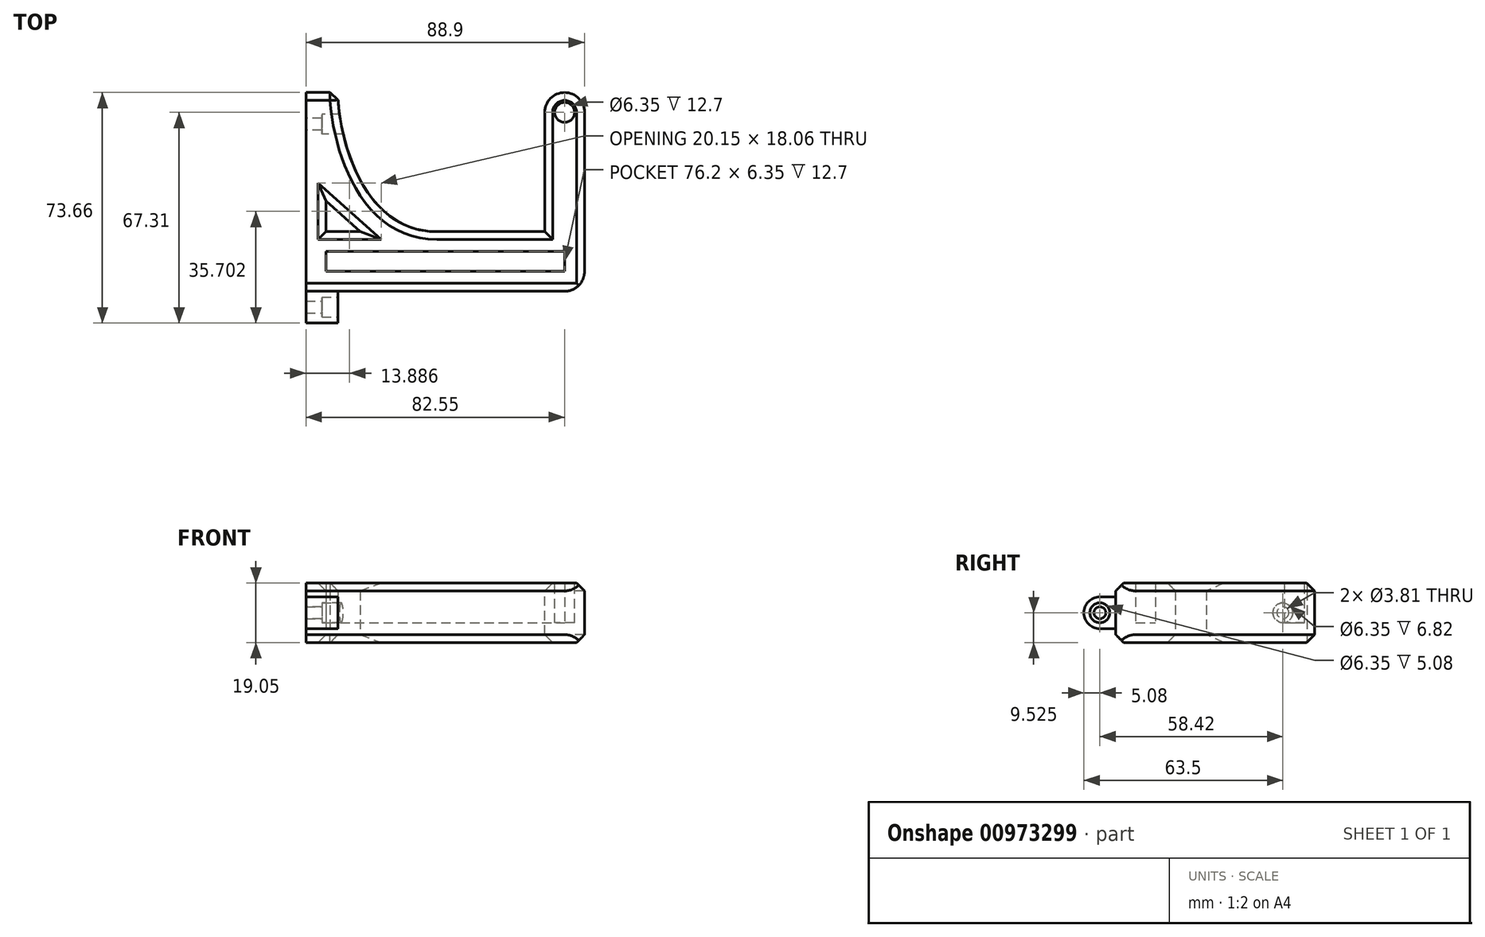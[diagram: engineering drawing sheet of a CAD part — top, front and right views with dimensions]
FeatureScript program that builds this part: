
annotation { "Feature Type Name" : "Feature", "Feature Type Description" : "" }
export const myFeature = defineFeature(function(context is Context, id is Id, definition is map)
    precondition{}
    {
        {
            var Q0;
            Q0=qCreatedBy(makeId("Top.planeOp"),FACE);
            var sketch = newSketch(context, id + "F0", { "sketchPlane" : qUnion([Q0])});
            skLineSegment(sketch, "E0.bottom", {"start": v(0, 0) * mm, "end": v(76.2, 0) * mm});
            skLineSegment(sketch, "E0.top", {"start": v(0, 6.35) * mm, "end": v(76.2, 6.35) * mm});
            skLineSegment(sketch, "E0.left", {"start": v(0, 0) * mm, "end": v(0, 6.35) * mm});
            skLineSegment(sketch, "E0.right", {"start": v(76.2, 0) * mm, "end": v(76.2, 6.35) * mm});
            skLineSegment(sketch, "E1.0", {"start": v(82.55, -6.35) * mm, "end": v(82.55, 12.7) * mm});
            skLineSegment(sketch, "E1.1", {"start": v(-6.35, -6.35) * mm, "end": v(82.55, -6.35) * mm});
            skLineSegment(sketch, "E1.2", {"start": v(-6.35, -6.35) * mm, "end": v(-6.35, 12.7) * mm});
            skLineSegment(sketch, "E1.3", {"start": v(31.6, 12.7) * mm, "end": v(82.55, 12.7) * mm});
            skLineSegment(sketch, "E2", {"start": v(-6.35, 12.7) * mm, "end": v(-6.35, 57.15) * mm});
            skLineSegment(sketch, "E3", {"start": v(-6.35, 57.15) * mm, "end": v(3.8, 57.15) * mm});
            skFitSpline(sketch, "E4", {"points": [v(3.8, 57.15) * mm, v(35.41, 12.7) * mm], "startDerivative": vector(0, -38.1) * mm, "endDerivative": vector(73.32, 0) * mm});
            skPoint(sketch, "E5.orphan", {"position": v(0, 12.7) * mm});
            skLineSegment(sketch, "E6", {"start": v(0, 22.54) * mm, "end": v(10.97, 12.7) * mm});
            skLineSegment(sketch, "E7", {"start": v(0, 22.54) * mm, "end": v(0, 12.7) * mm});
            skLineSegment(sketch, "E8", {"start": v(0, 12.7) * mm, "end": v(10.97, 12.7) * mm});
            skSolve(sketch);
        }
        {
            var Q0;
            Q0 = qSketchRegion(id + "F0", true);
            extrude(context, id + "F1", {"entities" : qUnion([Q0]), "depth" : 19.05 * mm, "offsetDistance" : 25.4 * mm});
        }
        {
            var Q0;
            Q0=makeQuery(id+"F0.imprint","IMPRINT",FACE,{"disambiguationData":[TD([[makeQuery(id+"F0.imprint","IMPRINT",EDGE,{"derivedFrom":sQuery(id+"F0.wireOp",EDGE,"E0.bottom")}),1.0]])]});
            extrude(context, id + "F2", {"entities" : qUnion([Q0]), "operationType" : NewBodyOperationType.ADD, "depth" : 6.35 * mm, "offsetDistance" : 25.4 * mm});
        }
        {
            var Q0;
            Q0=makeQuery(id+"F1.opExtrude","SWEPT_FACE",FACE,{"disambiguationData":[OSD([sQuery(id+"F0.wireOp",EDGE,"E1.2"),sQuery(id+"F0.wireOp",EDGE,"E2")])]});
            var sketch = newSketch(context, id + "F3", { "sketchPlane" : qUnion([Q0])});
            skCircle(sketch, "E9", {"center": v(-46.99, 9.53) * mm, "radius": 3.18 * mm});
            skPoint(sketch, "E9.centerSnap0", {"position": v(-57.15, 9.53) * mm});
            skCircle(sketch, "E10", {"center": v(-46.99, 9.53) * mm, "radius": 1.9 * mm});
            skSolve(sketch);
        }
        {
            var Q0;
            Q0=makeQuery(id+"F3.imprint","IMPRINT",FACE,{"disambiguationData":[TD([[makeQuery(id+"F3.imprint","IMPRINT",EDGE,{"derivedFrom":sQuery(id+"F3.wireOp",EDGE,"E9")}),1.0]])]});
            extrude(context, id + "F4", {"entities" : qUnion([Q0]), "operationType" : NewBodyOperationType.REMOVE, "endBound" : BoundingType.UP_TO_NEXT, "oppositeDirection" : true, "depth" : 25.4 * mm, "offsetDistance" : 25.4 * mm, "hasSecondDirection" : true, "secondDirectionOppositeDirection" : true, "secondDirectionDepth" : 5.08 * mm});
        }
        {
            var Q0;
            Q0=makeQuery(id+"F1.opExtrude","SWEPT_FACE",FACE,{"disambiguationData":[OSD([sQuery(id+"F0.wireOp",EDGE,"E1.2"),sQuery(id+"F0.wireOp",EDGE,"E2")])]});
            var sketch = newSketch(context, id + "F5", { "sketchPlane" : qUnion([Q0])});
            skLineSegment(sketch, "E11", {"start": v(6.35, 9.53) * mm, "end": v(17.62, 9.53) * mm, "construction": true});
            skLineSegment(sketch, "E12", {"start": v(6.35, 14.6) * mm, "end": v(11.43, 14.6) * mm});
            skLineSegment(sketch, "E13.MirrorCS", {"start": v(6.35, 4.45) * mm, "end": v(11.43, 4.45) * mm});
            skArc(sketch, "E14", {"start": v(11.43, 4.45) * mm, "mid": v(16.5, 9.53) * mm, "end": v(11.43, 14.6) * mm});
            skSolve(sketch);
        }
        {
            var Q0;
            Q0 = qSketchRegion(id + "F5", true);
            var Q1;
            {var subQ0=sQuery(id+"F5.wireOp",EDGE,"E12");Q1=makeQuery(id+"F5.imprint","IMPRINT",FACE,{"disambiguationData":[TD([[makeQuery(id+"F5.imprint","IMPRINT",EDGE,{"derivedFrom":subQ0}),-1.0]])]});}
            extrude(context, id + "F6", {"entities" : qUnion([Q0, Q1]), "operationType" : NewBodyOperationType.ADD, "oppositeDirection" : true, "depth" : 10.16 * mm, "offsetDistance" : 25.4 * mm});
        }
        {
            var Q0;
            Q0=makeQuery(id+"F6.opExtrude","CAP_FACE",FACE,{"disambiguationData":[OSD([sQuery(id+"F0.wireOp",EDGE,"E1.1"),sQuery(id+"F0.wireOp",EDGE,"E1.2"),sQuery(id+"F5.wireOp",EDGE,"E12"),sQuery(id+"F5.wireOp",EDGE,"E13.MirrorCS"),sQuery(id+"F5.wireOp",EDGE,"E14")])],"isStart":false});
            var sketch = newSketch(context, id + "F7", { "sketchPlane" : qUnion([Q0])});
            skCircle(sketch, "E15", {"center": v(-11.43, 9.53) * mm, "radius": 3.18 * mm});
            skCircle(sketch, "E16", {"center": v(-11.43, 9.53) * mm, "radius": 1.9 * mm});
            skSolve(sketch);
        }
        {
            var Q0;
            Q0 = qSketchRegion(id + "F7", true);
            extrude(context, id + "F8", {"entities" : qUnion([Q0]), "operationType" : NewBodyOperationType.REMOVE, "oppositeDirection" : true, "depth" : 5.08 * mm, "offsetDistance" : 25.4 * mm});
        }
        {
            var Q0;
            Q0=makeQuery(id+"F7.imprint","IMPRINT",FACE,{"disambiguationData":[TD([[makeQuery(id+"F7.imprint","IMPRINT",EDGE,{"derivedFrom":sQuery(id+"F7.wireOp",EDGE,"E16")}),1.0]])]});
            extrude(context, id + "F9", {"entities" : qUnion([Q0]), "operationType" : NewBodyOperationType.REMOVE, "endBound" : BoundingType.THROUGH_ALL, "oppositeDirection" : true, "depth" : 25.4 * mm, "offsetDistance" : 25.4 * mm});
        }
        {
            var Q0;
            Q0=makeQuery(id+"F3.imprint","IMPRINT",FACE,{"disambiguationData":[TD([[makeQuery(id+"F3.imprint","IMPRINT",EDGE,{"derivedFrom":sQuery(id+"F3.wireOp",EDGE,"E10")}),1.0]])]});
            var Q1;
            Q1=sQuery(id+"F3.wireOp",EDGE,"E10");
            extrude(context, id + "F10", {"entities" : qUnion([Q0]), "operationType" : NewBodyOperationType.REMOVE, "surfaceEntities" : qUnion([Q1]), "endBound" : BoundingType.THROUGH_ALL, "oppositeDirection" : true, "depth" : 25.4 * mm, "offsetDistance" : 25.4 * mm});
        }
        {
            var Q0;
            Q0=makeQuery(id+"F1.opExtrude","CAP_FACE",FACE,{"disambiguationData":[OSD([sQuery(id+"F0.wireOp",EDGE,"E0.bottom"),sQuery(id+"F0.wireOp",EDGE,"E0.top"),sQuery(id+"F0.wireOp",EDGE,"E0.left"),sQuery(id+"F0.wireOp",EDGE,"E0.right"),sQuery(id+"F0.wireOp",EDGE,"E1.0"),sQuery(id+"F0.wireOp",EDGE,"E1.1"),sQuery(id+"F0.wireOp",EDGE,"E1.2"),sQuery(id+"F0.wireOp",EDGE,"E1.3"),sQuery(id+"F0.wireOp",EDGE,"E2"),sQuery(id+"F0.wireOp",EDGE,"E3"),sQuery(id+"F0.wireOp",EDGE,"E4"),sQuery(id+"F0.wireOp",EDGE,"E6"),sQuery(id+"F0.wireOp",EDGE,"E7"),sQuery(id+"F0.wireOp",EDGE,"E8")])],"isStart":false});
            var sketch = newSketch(context, id + "F11", { "sketchPlane" : qUnion([Q0])});
            skLineSegment(sketch, "E17", {"start": v(82.55, 12.7) * mm, "end": v(82.55, 50.8) * mm});
            skLineSegment(sketch, "E18", {"start": v(69.85, 12.7) * mm, "end": v(69.85, 50.8) * mm});
            skLineSegment(sketch, "E19", {"start": v(82.55, 12.7) * mm, "end": v(69.85, 12.7) * mm});
            skArc(sketch, "E20", {"start": v(82.55, 50.8) * mm, "mid": v(76.2, 57.15) * mm, "end": v(69.85, 50.8) * mm});
            skSolve(sketch);
        }
        {
            var Q0;
            Q0=makeQuery(id+"F11.imprint","IMPRINT",FACE,{"disambiguationData":[TD([[makeQuery(id+"F11.imprint","IMPRINT",EDGE,{"derivedFrom":sQuery(id+"F11.wireOp",EDGE,"E17")}),1.0]])]});
            var Q1;
            {var subQ0=sQuery(id+"F0.wireOp",EDGE,"E0.right");var subQ1=sQuery(id+"F0.wireOp",EDGE,"E0.left");var subQ2=sQuery(id+"F0.wireOp",EDGE,"E0.top");var subQ3=sQuery(id+"F0.wireOp",EDGE,"E0.bottom");Q1=makeQuery(id+"F2.boolean.opBoolean","MERGE",FACE,{"derivedFrom":[makeQuery(id+"F1.opExtrude","CAP_FACE",FACE,{"disambiguationData":[OSD([subQ3,subQ2,subQ1,subQ0,sQuery(id+"F0.wireOp",EDGE,"E1.0"),sQuery(id+"F0.wireOp",EDGE,"E1.1"),sQuery(id+"F0.wireOp",EDGE,"E1.2"),sQuery(id+"F0.wireOp",EDGE,"E1.3"),sQuery(id+"F0.wireOp",EDGE,"E2"),sQuery(id+"F0.wireOp",EDGE,"E3"),sQuery(id+"F0.wireOp",EDGE,"E4"),sQuery(id+"F0.wireOp",EDGE,"E6"),sQuery(id+"F0.wireOp",EDGE,"E7"),sQuery(id+"F0.wireOp",EDGE,"E8")])],"isStart":true}),makeQuery(id+"F2.opExtrude","CAP_FACE",FACE,{"disambiguationData":[OSD([subQ3,subQ2,subQ1,subQ0])],"isStart":true})]});}
            extrude(context, id + "F12", {"entities" : qUnion([Q0]), "operationType" : NewBodyOperationType.ADD, "endBound" : BoundingType.UP_TO_SURFACE, "oppositeDirection" : true, "depth" : 25.4 * mm, "endBoundEntityFace" : qUnion([Q1]), "offsetDistance" : 25.4 * mm});
        }
        {
            var Q0;
            Q0=makeQuery(id+"F12.boolean.opBoolean","MERGE",FACE,{"derivedFrom":[makeQuery(id+"F1.opExtrude","CAP_FACE",FACE,{"disambiguationData":[OSD([sQuery(id+"F0.wireOp",EDGE,"E0.bottom"),sQuery(id+"F0.wireOp",EDGE,"E0.top"),sQuery(id+"F0.wireOp",EDGE,"E0.left"),sQuery(id+"F0.wireOp",EDGE,"E0.right"),sQuery(id+"F0.wireOp",EDGE,"E1.0"),sQuery(id+"F0.wireOp",EDGE,"E1.1"),sQuery(id+"F0.wireOp",EDGE,"E1.2"),sQuery(id+"F0.wireOp",EDGE,"E1.3"),sQuery(id+"F0.wireOp",EDGE,"E2"),sQuery(id+"F0.wireOp",EDGE,"E3"),sQuery(id+"F0.wireOp",EDGE,"E4"),sQuery(id+"F0.wireOp",EDGE,"E6"),sQuery(id+"F0.wireOp",EDGE,"E7"),sQuery(id+"F0.wireOp",EDGE,"E8")])],"isStart":false}),makeQuery(id+"F12.opExtrude","CAP_FACE",FACE,{"disambiguationData":[OSD([sQuery(id+"F11.wireOp",EDGE,"E17"),sQuery(id+"F11.wireOp",EDGE,"E18"),sQuery(id+"F11.wireOp",EDGE,"E19"),sQuery(id+"F11.wireOp",EDGE,"E20")])],"isStart":true})]});
            var sketch = newSketch(context, id + "F13", { "sketchPlane" : qUnion([Q0])});
            skCircle(sketch, "E21", {"center": v(76.2, 50.8) * mm, "radius": 3.18 * mm});
            skSolve(sketch);
        }
        {
            var Q0;
            Q0 = qSketchRegion(id + "F13", true);
            var Q1;
            Q1=makeQuery(id+"F2.opExtrude","CAP_FACE",FACE,{"disambiguationData":[OSD([sQuery(id+"F0.wireOp",EDGE,"E0.bottom"),sQuery(id+"F0.wireOp",EDGE,"E0.top"),sQuery(id+"F0.wireOp",EDGE,"E0.left"),sQuery(id+"F0.wireOp",EDGE,"E0.right")])],"isStart":false});
            extrude(context, id + "F14", {"entities" : qUnion([Q0]), "operationType" : NewBodyOperationType.REMOVE, "endBound" : BoundingType.UP_TO_SURFACE, "oppositeDirection" : true, "depth" : 12.7 * mm, "endBoundEntityFace" : qUnion([Q1]), "offsetDistance" : 25.4 * mm});
        }
        {
            var Q0;
            Q0=makeQuery(id+"F1.opExtrude","CAP_EDGE",EDGE,{"disambiguationData":[OSD([sQuery(id+"F0.wireOp",EDGE,"E1.3")])],"isStart":true});
            var Q1;
            Q1=makeQuery(id+"F1.opExtrude","CAP_EDGE",EDGE,{"disambiguationData":[OSD([sQuery(id+"F0.wireOp",EDGE,"E1.3")])],"isStart":false});
            var Q2;
            Q2=makeQuery(id+"F1.opExtrude","CAP_EDGE",EDGE,{"disambiguationData":[OSD([sQuery(id+"F0.wireOp",EDGE,"E1.1")])],"isStart":true});
            var Q3;
            Q3=makeQuery(id+"F1.opExtrude","CAP_EDGE",EDGE,{"disambiguationData":[OSD([sQuery(id+"F0.wireOp",EDGE,"E1.1")])],"isStart":false});
            var Q4;
            Q4=makeQuery(id+"F12.boolean.opBoolean","MERGE",EDGE,{"derivedFrom":[makeQuery(id+"F1.opExtrude","CAP_EDGE",EDGE,{"disambiguationData":[OSD([sQuery(id+"F0.wireOp",EDGE,"E1.0")])],"isStart":true}),makeQuery(id+"F12.opExtrude","CAP_EDGE",EDGE,{"disambiguationData":[OSD([sQuery(id+"F11.wireOp",EDGE,"E17")])],"isStart":false})]});
            var Q5;
            Q5=makeQuery(id+"F12.boolean.opBoolean","MERGE",EDGE,{"derivedFrom":[makeQuery(id+"F1.opExtrude","CAP_EDGE",EDGE,{"disambiguationData":[OSD([sQuery(id+"F0.wireOp",EDGE,"E1.0")])],"isStart":false}),makeQuery(id+"F12.opExtrude","CAP_EDGE",EDGE,{"disambiguationData":[OSD([sQuery(id+"F11.wireOp",EDGE,"E17")])],"isStart":true})]});
            var Q6;
            Q6=makeQuery(id+"F1.opExtrude","SWEPT_EDGE",EDGE,{"disambiguationData":[OSD([sQuery(id+"F0.wireOp",EDGE,"E3"),sQuery(id+"F0.wireOp",EDGE,"E4")])]});
            var Q7;
            Q7=makeQuery(id+"F1.opExtrude","CAP_EDGE",EDGE,{"disambiguationData":[OSD([sQuery(id+"F0.wireOp",EDGE,"E6")])],"isStart":true});
            var Q8;
            Q8=makeQuery(id+"F1.opExtrude","CAP_EDGE",EDGE,{"disambiguationData":[OSD([sQuery(id+"F0.wireOp",EDGE,"E8")])],"isStart":true});
            var Q9;
            Q9=makeQuery(id+"F1.opExtrude","CAP_EDGE",EDGE,{"disambiguationData":[OSD([sQuery(id+"F0.wireOp",EDGE,"E7")])],"isStart":true});
            var Q10;
            Q10=makeQuery(id+"F1.opExtrude","CAP_EDGE",EDGE,{"disambiguationData":[OSD([sQuery(id+"F0.wireOp",EDGE,"E7")])],"isStart":false});
            var Q11;
            Q11=makeQuery(id+"F1.opExtrude","CAP_EDGE",EDGE,{"disambiguationData":[OSD([sQuery(id+"F0.wireOp",EDGE,"E8")])],"isStart":false});
            var Q12;
            Q12=makeQuery(id+"F1.opExtrude","CAP_EDGE",EDGE,{"disambiguationData":[OSD([sQuery(id+"F0.wireOp",EDGE,"E6")])],"isStart":false});
            var Q13;
            Q13=makeQuery(id+"F1.opExtrude","CAP_EDGE",EDGE,{"disambiguationData":[OSD([sQuery(id+"F0.wireOp",EDGE,"E3")])],"isStart":false});
            var Q14;
            Q14=makeQuery(id+"F1.opExtrude","CAP_EDGE",EDGE,{"disambiguationData":[OSD([sQuery(id+"F0.wireOp",EDGE,"E3")])],"isStart":true});
            chamfer(context, id + "F15", {"entities" : qUnion([Q0, Q1, Q2, Q3, Q4, Q5, Q6, Q7, Q8, Q9, Q10, Q11, Q12, Q13, Q14]), "chamferType" : ChamferType.OFFSET_ANGLE, "width" : 2.54 * mm, "oppositeDirection" : false, "angle" : 45 * degree, "tangentPropagation" : true});
        }
        {
            var Q0;
            Q0=makeQuery(id+"F1.opExtrude","SWEPT_EDGE",EDGE,{"disambiguationData":[OSD([sQuery(id+"F0.wireOp",EDGE,"E1.0"),sQuery(id+"F0.wireOp",EDGE,"E1.1")])]});
            fillet(context, id + "F16", {"entities" : qUnion([Q0]), "radius" : 6.35 * mm, "tangentPropagation" : true, "allowEdgeOverflow" : false});
        }
    });
